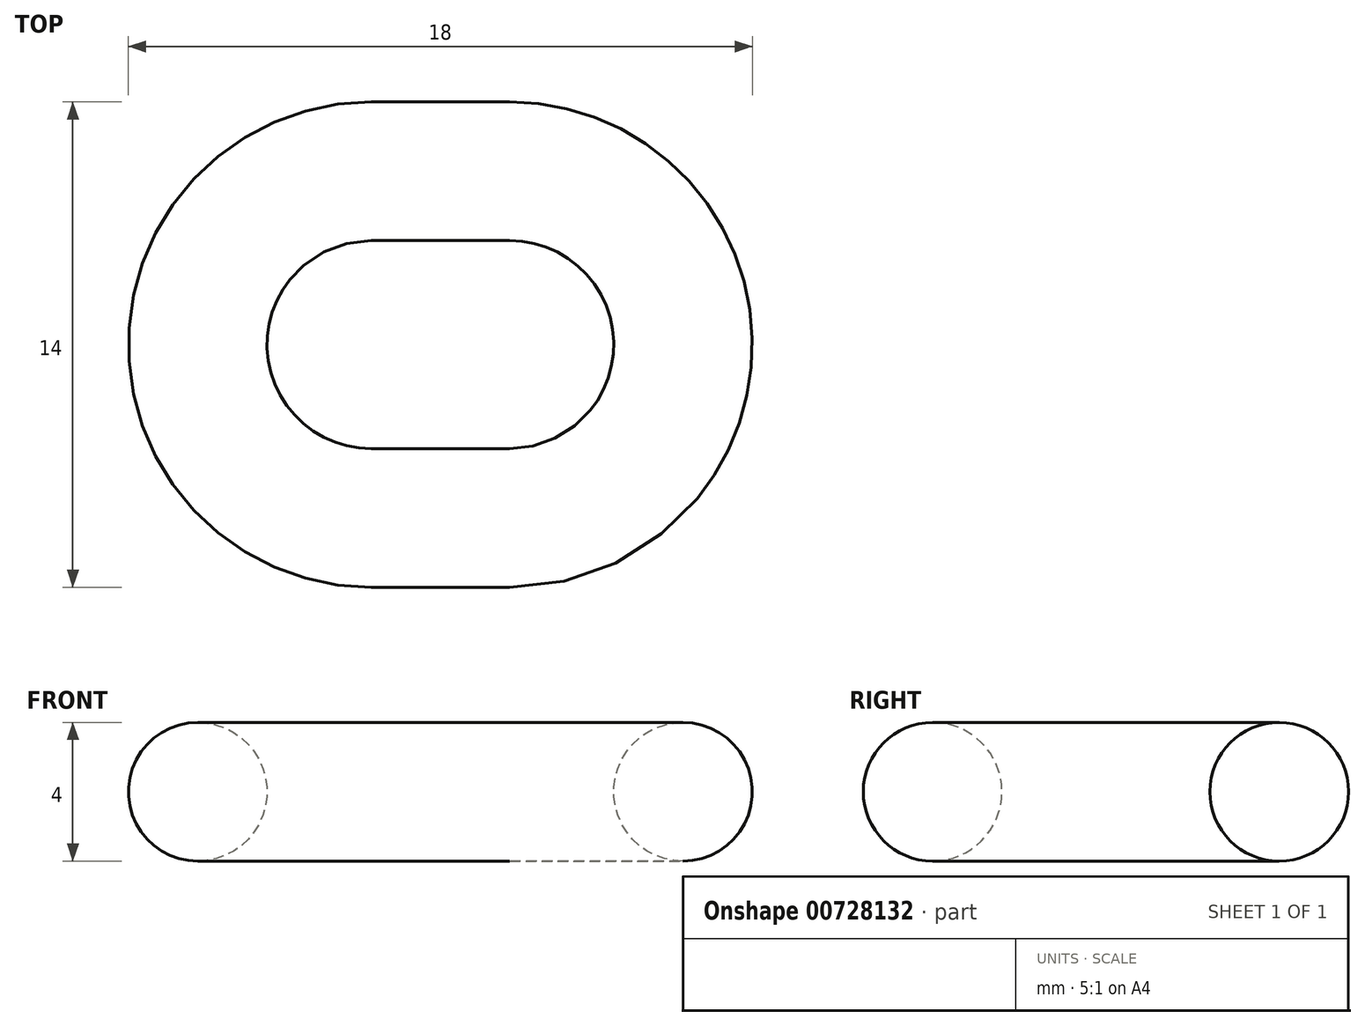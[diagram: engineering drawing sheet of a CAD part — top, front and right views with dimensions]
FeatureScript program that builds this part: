
annotation { "Feature Type Name" : "Feature", "Feature Type Description" : "" }
export const myFeature = defineFeature(function(context is Context, id is Id, definition is map)
    precondition{}
    {
        {
            var Q0;
            Q0=qCreatedBy(makeId("Top.planeOp"),FACE);
            var sketch = newSketch(context, id + "F0", { "sketchPlane" : qUnion([Q0])});
            skLineSegment(sketch, "E0", {"start": v(0, 0) * mm, "end": v(4, 0) * mm, "construction": true});
            skArc(sketch, "E1.0.startCap", {"start": v(0, -5) * mm, "mid": v(-5, 0) * mm, "end": v(0, 5) * mm});
            skArc(sketch, "E1.0.endCap", {"start": v(4, 5) * mm, "mid": v(9, 0) * mm, "end": v(4, -5) * mm});
            skLineSegment(sketch, "E1.0.left", {"start": v(0, 5) * mm, "end": v(4, 5) * mm});
            skLineSegment(sketch, "E1.0.right", {"start": v(0, -5) * mm, "end": v(4, -5) * mm});
            skArc(sketch, "E2.0.startCap", {"start": v(0, -7) * mm, "mid": v(-7, 0) * mm, "end": v(0, 7) * mm, "construction": true});
            skArc(sketch, "E2.0.endCap", {"start": v(4, 7) * mm, "mid": v(11, 0) * mm, "end": v(4, -7) * mm, "construction": true});
            skLineSegment(sketch, "E2.0.left", {"start": v(0, 7) * mm, "end": v(4, 7) * mm, "construction": true});
            skLineSegment(sketch, "E2.0.right", {"start": v(0, -7) * mm, "end": v(4, -7) * mm, "construction": true});
            skLineSegment(sketch, "E3", {"start": v(-7, 0) * mm, "end": v(-7, 19.46) * mm, "construction": true});
            skLineSegment(sketch, "E4", {"start": v(11, 0) * mm, "end": v(11, 17.21) * mm, "construction": true});
            skSolve(sketch);
        }
        {
            var Q0;
            Q0=qCreatedBy(makeId("Right.planeOp"),FACE);
            var sketch = newSketch(context, id + "F1", { "sketchPlane" : qUnion([Q0])});
            skCircle(sketch, "E5", {"center": v(-5, 0) * mm, "radius": 2 * mm});
            skSolve(sketch);
        }
        {
            var Q0;
            Q0=makeQuery(id+"F1.imprint","IMPRINT",FACE,{"disambiguationData":[TD([[makeQuery(id+"F1.imprint","IMPRINT",EDGE,{"derivedFrom":sQuery(id+"F1.wireOp",EDGE,"E5")}),1.0]])]});
            var Q1;
            Q1=sQuery(id+"F0.wireOp",EDGE,"E1.0.right");
            var Q2;
            Q2=sQuery(id+"F0.wireOp",EDGE,"E1.0.endCap");
            var Q3;
            Q3=sQuery(id+"F0.wireOp",EDGE,"E1.0.left");
            var Q4;
            Q4=sQuery(id+"F0.wireOp",EDGE,"E1.0.startCap");
            sweep(context, id + "F2", {"profiles" : qUnion([Q0]), "path" : qUnion([Q1, Q2, Q3, Q4])});
        }
    });
